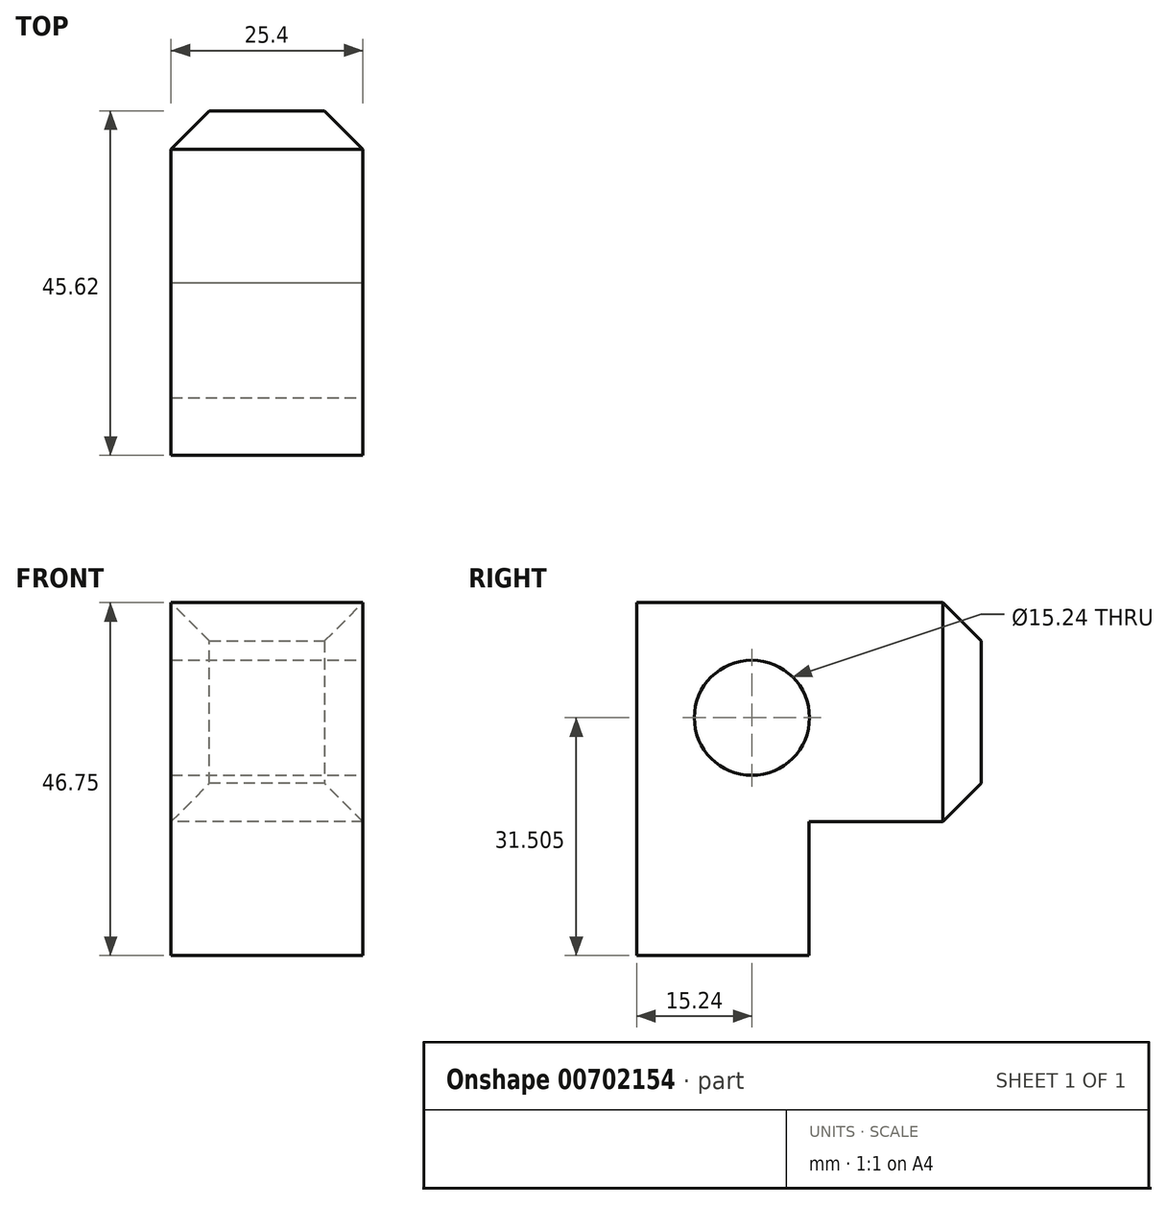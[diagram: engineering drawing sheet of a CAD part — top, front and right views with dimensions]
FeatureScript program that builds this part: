
annotation { "Feature Type Name" : "Feature", "Feature Type Description" : "" }
export const myFeature = defineFeature(function(context is Context, id is Id, definition is map)
    precondition{}
    {
        {
            var Q0;
            Q0=qCreatedBy(makeId("Right.planeOp"),FACE);
            var sketch = newSketch(context, id + "F0", { "sketchPlane" : qUnion([Q0])});
            skLineSegment(sketch, "E0", {"start": v(0, 0) * mm, "end": v(0, 46.75) * mm});
            skLineSegment(sketch, "E1", {"start": v(0, 46.75) * mm, "end": v(45.62, 46.75) * mm});
            skLineSegment(sketch, "E2", {"start": v(45.62, 46.75) * mm, "end": v(45.62, 17.72) * mm});
            skLineSegment(sketch, "E3", {"start": v(45.62, 17.72) * mm, "end": v(22.82, 17.72) * mm});
            skLineSegment(sketch, "E4", {"start": v(22.82, 17.72) * mm, "end": v(22.82, 0) * mm});
            skLineSegment(sketch, "E5", {"start": v(22.82, 0) * mm, "end": v(0, 0) * mm});
            skSolve(sketch);
        }
        {
            var Q0;
            Q0 = qSketchRegion(id + "F0", true);
            extrude(context, id + "F1", {"entities" : qUnion([Q0]), "depth" : 25.4 * mm, "offsetDistance" : 25.4 * mm});
        }
        {
            var Q0;
            Q0=makeQuery(id+"F1.opExtrude","CAP_FACE",FACE,{"disambiguationData":[OSD([sQuery(id+"F0.wireOp",EDGE,"E0"),sQuery(id+"F0.wireOp",EDGE,"E1"),sQuery(id+"F0.wireOp",EDGE,"E2"),sQuery(id+"F0.wireOp",EDGE,"E3"),sQuery(id+"F0.wireOp",EDGE,"E4"),sQuery(id+"F0.wireOp",EDGE,"E5")])],"isStart":false});
            var sketch = newSketch(context, id + "F2", { "sketchPlane" : qUnion([Q0])});
            skCircle(sketch, "E6", {"center": v(15.24, 31.5) * mm, "radius": 6.42 * mm});
            skSolve(sketch);
        }
        {
            var Q0;
            Q0=sQuery(id+"F2.wireOp",VERTEX,"E6.center");
            var Q1;
            Q1=makeQuery(id+"F1.opExtrude","SWEPT_BODY",BODY,{"disambiguationData":[OSD([sQuery(id+"F0.wireOp",EDGE,"E0"),sQuery(id+"F0.wireOp",EDGE,"E1"),sQuery(id+"F0.wireOp",EDGE,"E2"),sQuery(id+"F0.wireOp",EDGE,"E3"),sQuery(id+"F0.wireOp",EDGE,"E4"),sQuery(id+"F0.wireOp",EDGE,"E5")])]});
            hole(context, id + "F3", {"style" : HoleStyle.SIMPLE, "endStyle" : HoleEndStyle.THROUGH, "holeDiameter" : 15.24 * mm, "majorDiameter" : 6.35 * mm, "isTappedThrough" : true, "tappedDepth" : 12.7 * mm, "tapClearance" : 3, "locations" : qUnion([Q0]), "scope" : qUnion([Q1])});
        }
        {
            var Q0;
            Q0=makeQuery(id+"F1.opExtrude","SWEPT_EDGE",EDGE,{"disambiguationData":[OSD([sQuery(id+"F0.wireOp",EDGE,"E2"),sQuery(id+"F0.wireOp",EDGE,"E3")])]});
            var Q1;
            Q1=makeQuery(id+"F1.opExtrude","CAP_EDGE",EDGE,{"disambiguationData":[OSD([sQuery(id+"F0.wireOp",EDGE,"E2")])],"isStart":true});
            var Q2;
            Q2=makeQuery(id+"F1.opExtrude","SWEPT_EDGE",EDGE,{"disambiguationData":[OSD([sQuery(id+"F0.wireOp",EDGE,"E1"),sQuery(id+"F0.wireOp",EDGE,"E2")])]});
            var Q3;
            Q3=makeQuery(id+"F1.opExtrude","CAP_EDGE",EDGE,{"disambiguationData":[OSD([sQuery(id+"F0.wireOp",EDGE,"E2")])],"isStart":false});
            chamfer(context, id + "F4", {"entities" : qUnion([Q0, Q1, Q2, Q3]), "width" : 5.08 * mm, "tangentPropagation" : true});
        }
    });
